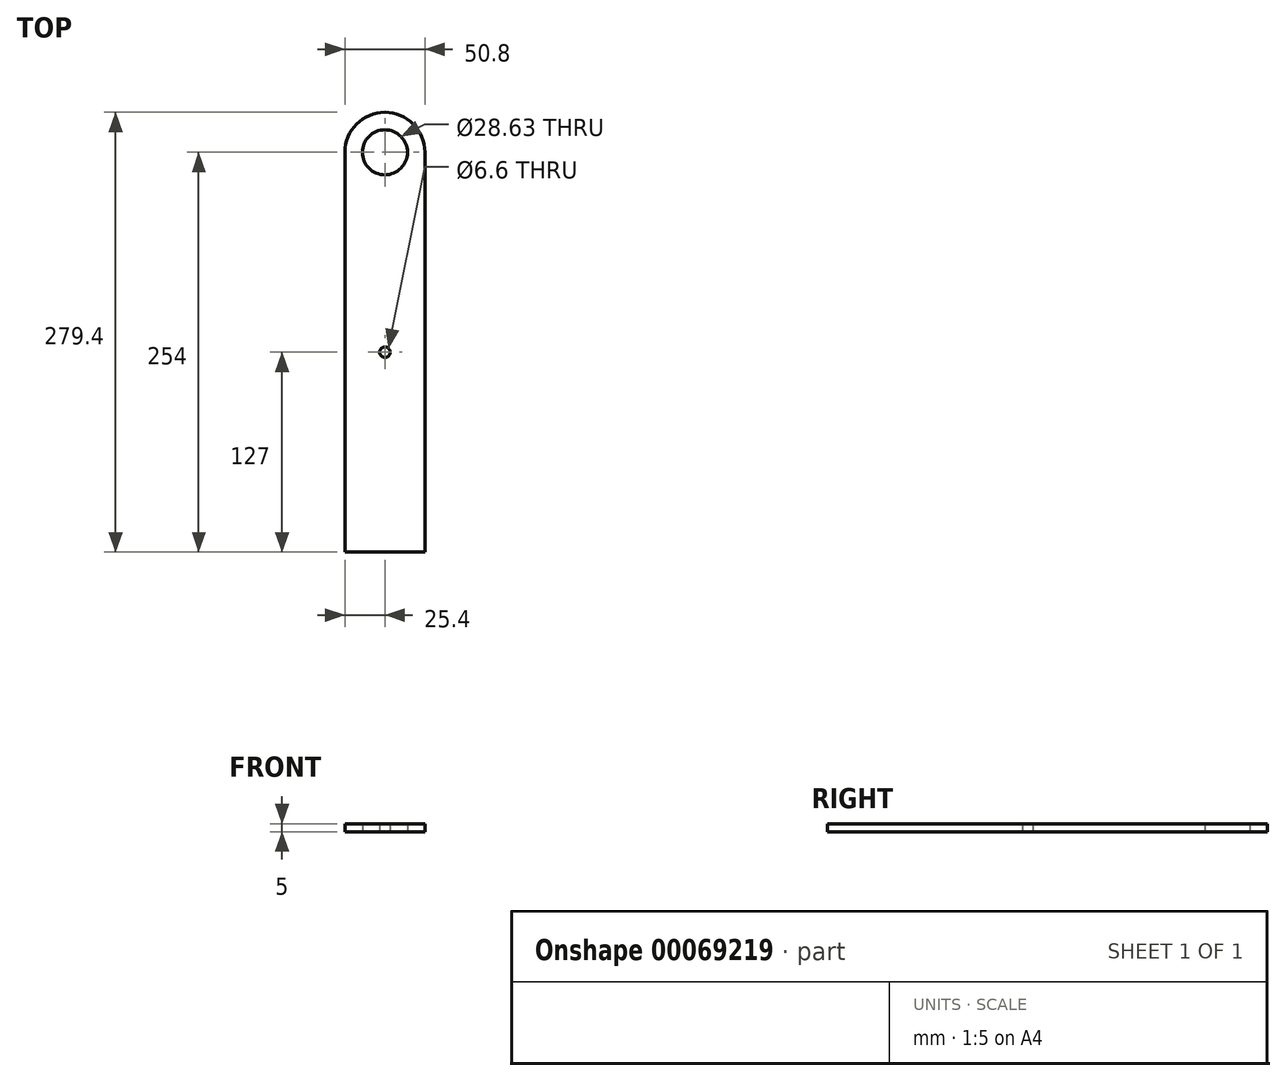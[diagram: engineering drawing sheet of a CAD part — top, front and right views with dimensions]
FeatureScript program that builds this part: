
annotation { "Feature Type Name" : "Feature", "Feature Type Description" : "" }
export const myFeature = defineFeature(function(context is Context, id is Id, definition is map)
    precondition{}
    {
        {
            var Q0;
            Q0=qCreatedBy(makeId("Top.planeOp"),FACE);
            var sketch = newSketch(context, id + "F0", { "sketchPlane" : qUnion([Q0])});
            skLineSegment(sketch, "E0.rect.top", {"start": v(25.4, -127) * mm, "end": v(-25.4, -127) * mm});
            skLineSegment(sketch, "E0.rect.left", {"start": v(25.4, 127) * mm, "end": v(25.4, -127) * mm});
            skLineSegment(sketch, "E0.rect.right", {"start": v(-25.4, 127) * mm, "end": v(-25.4, -127) * mm});
            skPoint(sketch, "E0.rect.middle", {"position": v(0, 0) * mm});
            skCircle(sketch, "E1", {"center": v(0, 127) * mm, "radius": 14.31 * mm});
            skArc(sketch, "E2", {"start": v(25.4, 127) * mm, "mid": v(0, 152.4) * mm, "end": v(-25.4, 127) * mm});
            skCircle(sketch, "E3", {"center": v(0, 0) * mm, "radius": 3.3 * mm});
            skSolve(sketch);
        }
        {
            var Q0;
            Q0=makeQuery(id+"F0.imprint","IMPRINT",FACE,{"disambiguationData":[TD([[makeQuery(id+"F0.imprint","IMPRINT",EDGE,{"derivedFrom":sQuery(id+"F0.wireOp",EDGE,"E0.rect.top")}),-1.0]])]});
            extrude(context, id + "F1", {"entities" : qUnion([Q0]), "depth" : 5 * mm});
        }
    });
